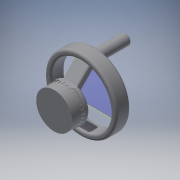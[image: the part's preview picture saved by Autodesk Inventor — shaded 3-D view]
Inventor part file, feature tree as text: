
AUTODESK INVENTOR PART (.ipt)
format: ipt  version: 2016 (Build 200138000, 138)  size: 548,864 bytes
history: native  units: mm
features: extrude x13, sketch x13, fillet x6, pattern_circular x1, chamfer x1, plane x1
ambient origin geometry x8: Origin, YZ Plane, XZ Plane, XY Plane, X Axis, Y Axis, Z Axis, Center Point
bodies: Solid1 (feature_tree)
feature tree (35):
  extrude  "Extrusion1"  Depth=20.0mm TaperAngle=0.0deg
  extrude  "Extrusion2"  Depth=5.0mm TaperAngle=0.0deg
  extrude  "Extrusion3"  Depth=5.0mm
  pattern_circular  "Circular Pattern1"  Count=30 Angle=360.0deg
  extrude  "Extrusion4"  Depth=10.0mm TaperAngle=0.0deg
  extrude  "Extrusion5"  Depth=16.0mm
  extrude  "Extrusion6"  Depth=10.0mm
  chamfer  "Chamfer1"  Distance=10.0mm
  plane  "Work Plane1"
  extrude  "Extrusion7"  Depth=2.0mm
  fillet  "Fillet1"  Radius=150.0mm
  extrude  "Extrusion8"  Depth=5.0mm TaperAngle=0.0deg
  fillet  "Fillet2"  Radius=5.0mm
  extrude  "Extrusion9"  Depth=5.0mm
  fillet  "Fillet3"  Radius=62.25mm
  extrude  "Extrusion10"  Depth=5.0mm TaperAngle=0.0deg
  fillet  "Fillet4"  Radius=4.0mm
  extrude  "Extrusion11"  Depth=4.0mm
  fillet  "Fillet5"  Radius=22.0mm
  extrude  "Extrusion12"  Depth=2.0mm TaperAngle=0.0deg
  extrude  "Extrusion13"  Depth=2.0mm
  fillet  "Fillet6"  [1 undecoded]
  sketch  "Sketch1"  dims[d0=75.0mm d1=20.0mm d2=0.0mm]
  sketch  "Sketch2"  dims[d3=76.0mm d4=5.0mm d5=0.0mm]
  sketch  "Sketch3"  dims[d7=2.5mm d8=5.0mm]
  sketch  "Sketch4"  dims[d9=5.0mm d10=0.0mm d11=300.0mm d12=360.0deg]
  sketch  "Sketch5"  dims[d14=78.0mm d15=10.0mm d16=0.0mm]
  sketch  "Sketch6"  dims[d17=16.0mm d18=16.0mm]
  sketch  "Sketch7"  dims[d19=10.0mm d20=0.0mm d21=55.0mm d22=10.0mm d23=0.0mm]
  sketch  "Sketch8"  dims[d24=10.0mm d25=2.0mm d26=45.0deg d27=50.0mm d28=150.0mm]
  sketch  "Sketch9"  dims[d29=125.0mm d30=30.0mm d31=0.0mm d32=5.0mm]
  sketch  "Sketch10"  dims[d33=61.75mm d34=0.0mm d35=5.0mm d36=62.25mm d37=0.0mm]
  sketch  "Sketch11"  dims[d38=5.0mm d39=32.0mm d40=0.0mm d41=4.0mm]
  sketch  "Sketch12"  dims[d42=32.0mm d43=0.0mm d44=4.0mm d45=22.0mm]
  sketch  "Sketch13"  dims[d46=50.0mm d47=0.0mm d48=40.0mm d49=0.0mm d50=2.0mm]
note: 1 required parameter value undecoded (feature->parameter linkage not recoverable at this tier; creation-order binding heuristic only, values carry confidence <= 0.55)
